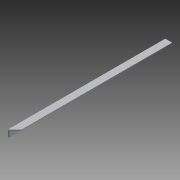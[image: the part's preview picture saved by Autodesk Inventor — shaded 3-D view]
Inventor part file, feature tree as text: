
AUTODESK INVENTOR PART (.ipt)
format: ipt  version: 2014 (Build 180170000, 170)  size: 81,408 bytes
history: native  units: in
note: dims shown in document units (in); Inventor stores cm internally (conversion verified against a paired STEP export)
features: extrude x2, sketch x2
ambient origin geometry x8: Origin, YZ Plane, XZ Plane, XY Plane, X Axis, Y Axis, Z Axis, Center Point
bodies: Solid1 (feature_tree)
feature tree (4):
  extrude  "Extrusion1"  Depth=0.5in
  extrude  "Extrusion3"  Depth=0.45in
  sketch  "Sketch1"  dims[d0=0.5in d1=0.5in]
  sketch  "Sketch3"  dims[d2=0.05in d3=0.45in d4=11.5in d5=0.0in d10=45.0deg d11=1.0in d12=0.0in]
